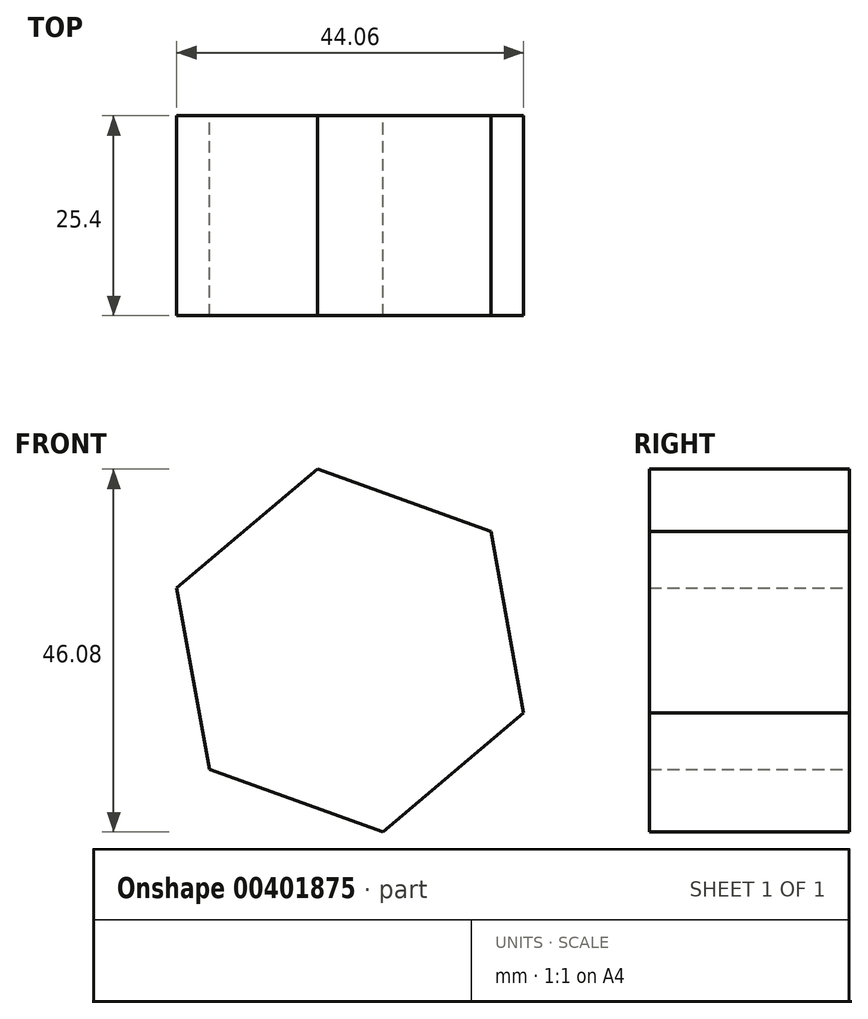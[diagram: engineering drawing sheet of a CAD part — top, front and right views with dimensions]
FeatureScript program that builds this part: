
annotation { "Feature Type Name" : "Feature", "Feature Type Description" : "" }
export const myFeature = defineFeature(function(context is Context, id is Id, definition is map)
    precondition{}
    {
        {
            var Q0;
            Q0=qCreatedBy(makeId("Front.planeOp"),FACE);
            var sketch = newSketch(context, id + "F0", { "sketchPlane" : qUnion([Q0])});
            skCircle(sketch, "E0.cCircle", {"center": v(-35.4, 31.7) * mm, "radius": 20.28 * mm, "construction": true});
            skLineSegment(sketch, "E0.0", {"start": v(-13.37, 23.78) * mm, "end": v(-31.25, 8.67) * mm});
            skLineSegment(sketch, "E0.1", {"start": v(-31.25, 8.67) * mm, "end": v(-53.28, 16.6) * mm});
            skLineSegment(sketch, "E0.2", {"start": v(-53.28, 16.6) * mm, "end": v(-57.43, 39.64) * mm});
            skLineSegment(sketch, "E0.3", {"start": v(-57.43, 39.64) * mm, "end": v(-39.54, 54.75) * mm});
            skLineSegment(sketch, "E0.4", {"start": v(-39.54, 54.75) * mm, "end": v(-17.51, 46.82) * mm});
            skLineSegment(sketch, "E0.5", {"start": v(-17.51, 46.82) * mm, "end": v(-13.37, 23.78) * mm});
            skPoint(sketch, "E0.0.midPoint", {"position": v(-22.3, 16.22) * mm});
            skSolve(sketch);
        }
        {
            var Q0;
            Q0 = qSketchRegion(id + "F0", true);
            extrude(context, id + "F1", {"entities" : qUnion([Q0]), "depth" : 25.4 * mm});
        }
    });
